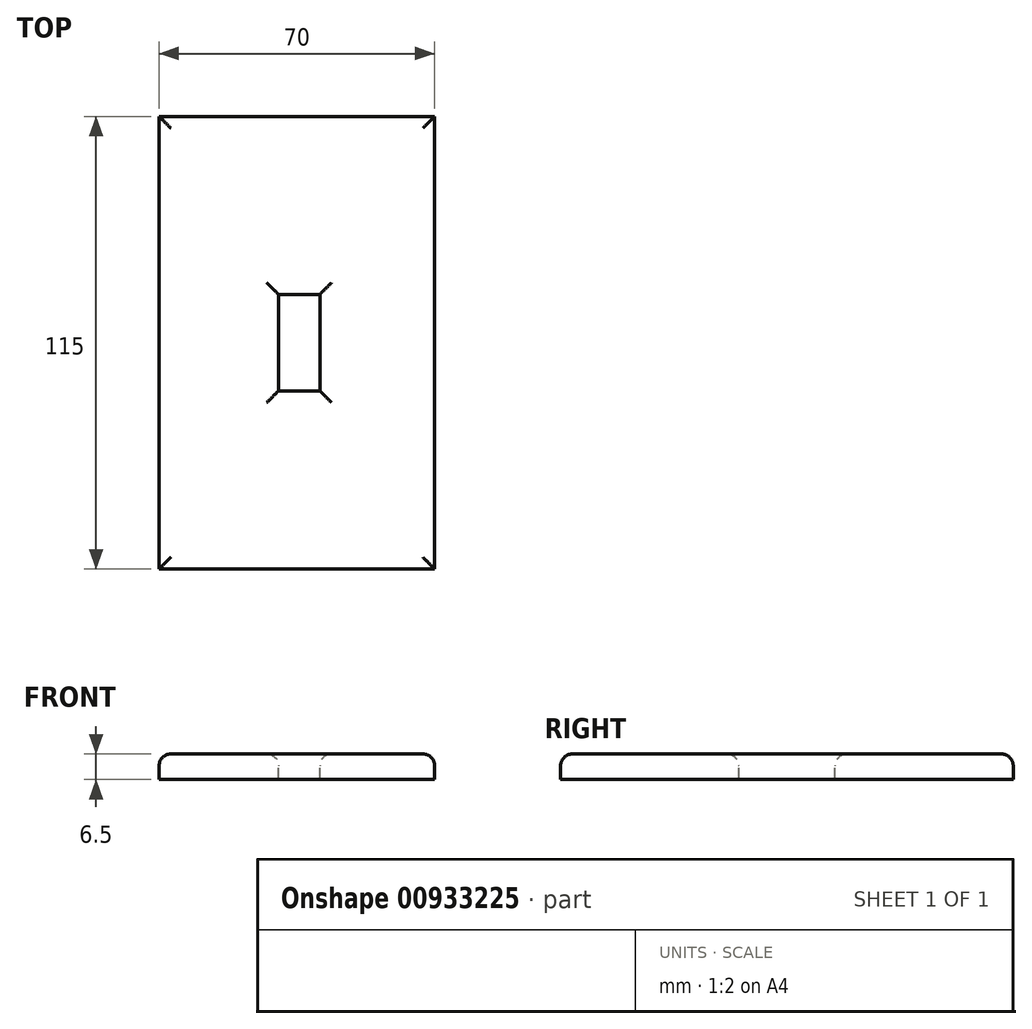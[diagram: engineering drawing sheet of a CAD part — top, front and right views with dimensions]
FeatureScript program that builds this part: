
annotation { "Feature Type Name" : "Feature", "Feature Type Description" : "" }
export const myFeature = defineFeature(function(context is Context, id is Id, definition is map)
    precondition{}
    {
        {
            var Q0;
            Q0=qCreatedBy(makeId("Top.planeOp"),FACE);
            var sketch = newSketch(context, id + "F0", { "sketchPlane" : qUnion([Q0])});
            skLineSegment(sketch, "E0.bottom", {"start": v(-34.97, 53.4) * mm, "end": v(35.03, 53.4) * mm});
            skLineSegment(sketch, "E0.top", {"start": v(-34.97, -61.6) * mm, "end": v(35.03, -61.6) * mm});
            skLineSegment(sketch, "E0.left", {"start": v(-34.97, 53.4) * mm, "end": v(-34.97, -61.6) * mm});
            skLineSegment(sketch, "E0.right", {"start": v(35.03, 53.4) * mm, "end": v(35.03, -61.6) * mm});
            skSolve(sketch);
        }
        {
            var Q0;
            Q0 = qSketchRegion(id + "F0", true);
            extrude(context, id + "F1", {"entities" : qUnion([Q0]), "depth" : 6.5 * mm, "offsetDistance" : 25.4 * mm});
        }
        {
            var Q0;
            Q0=makeQuery(id+"F1.opExtrude","CAP_FACE",FACE,{"disambiguationData":[OSD([sQuery(id+"F0.wireOp",EDGE,"E0.bottom"),sQuery(id+"F0.wireOp",EDGE,"E0.top"),sQuery(id+"F0.wireOp",EDGE,"E0.left"),sQuery(id+"F0.wireOp",EDGE,"E0.right")])],"isStart":false});
            var sketch = newSketch(context, id + "F2", { "sketchPlane" : qUnion([Q0])});
            skLineSegment(sketch, "E1.bottom", {"start": v(-4.64, 8.15) * mm, "end": v(5.86, 8.15) * mm});
            skLineSegment(sketch, "E1.top", {"start": v(-4.64, -16.35) * mm, "end": v(5.86, -16.35) * mm});
            skLineSegment(sketch, "E1.left", {"start": v(-4.64, 8.15) * mm, "end": v(-4.64, -16.35) * mm});
            skLineSegment(sketch, "E1.right", {"start": v(5.86, 8.15) * mm, "end": v(5.86, -16.35) * mm});
            skSolve(sketch);
        }
        {
            var Q0;
            Q0 = qSketchRegion(id + "F2", true);
            var Q1;
            Q1=makeQuery(id+"F1.opExtrude","CAP_FACE",FACE,{"disambiguationData":[OSD([sQuery(id+"F0.wireOp",EDGE,"E0.bottom"),sQuery(id+"F0.wireOp",EDGE,"E0.top"),sQuery(id+"F0.wireOp",EDGE,"E0.left"),sQuery(id+"F0.wireOp",EDGE,"E0.right")])],"isStart":true});
            extrude(context, id + "F3", {"entities" : qUnion([Q0]), "operationType" : NewBodyOperationType.REMOVE, "endBound" : BoundingType.UP_TO_SURFACE, "oppositeDirection" : true, "depth" : 25.4 * mm, "endBoundEntityFace" : qUnion([Q1]), "offsetDistance" : 25.4 * mm});
        }
        {
            var Q0;
            Q0=makeQuery(id+"F1.opExtrude","CAP_FACE",FACE,{"disambiguationData":[OSD([sQuery(id+"F0.wireOp",EDGE,"E0.bottom"),sQuery(id+"F0.wireOp",EDGE,"E0.top"),sQuery(id+"F0.wireOp",EDGE,"E0.left"),sQuery(id+"F0.wireOp",EDGE,"E0.right")])],"isStart":false});
            fillet(context, id + "F4", {"entities" : qUnion([Q0]), "radius" : 3 * mm, "tangentPropagation" : true, "allowEdgeOverflow" : false});
        }
    });
